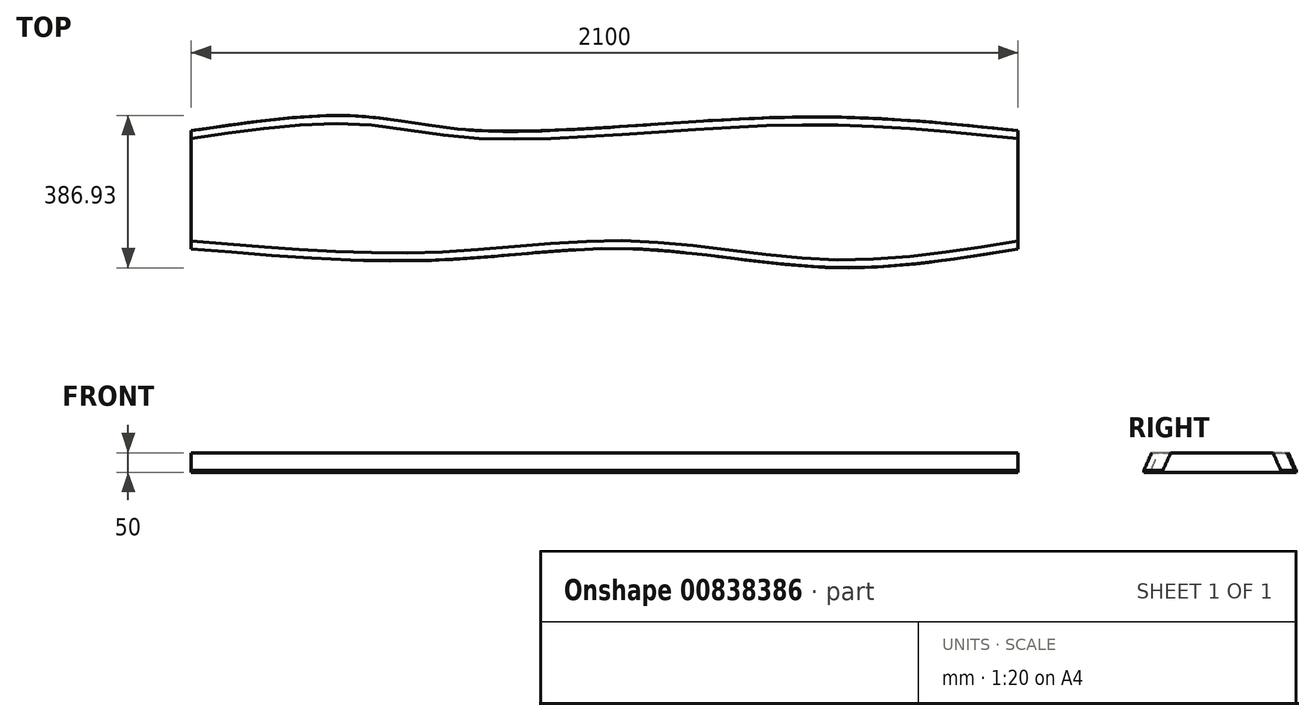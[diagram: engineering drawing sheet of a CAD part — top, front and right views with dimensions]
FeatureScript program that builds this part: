
annotation { "Feature Type Name" : "Feature", "Feature Type Description" : "" }
export const myFeature = defineFeature(function(context is Context, id is Id, definition is map)
    precondition{}
    {
        {
            var Q0;
            Q0=qCreatedBy(makeId("Top.planeOp"),FACE);
            var sketch = newSketch(context, id + "F0", { "sketchPlane" : qUnion([Q0])});
            skLineSegment(sketch, "E0.left", {"start": v(0, 0) * mm, "end": v(0, 300) * mm});
            skLineSegment(sketch, "E0.right", {"start": v(2100, 0) * mm, "end": v(2100, 300) * mm});
            skFitSpline(sketch, "E1", {"points": [v(0, 300) * mm, v(410.68, 337.9) * mm, v(739.53, 300) * mm, v(1506.84, 334.12) * mm, v(2100, 300) * mm], "startDerivative": vector(1943.02, 290.28) * mm, "endDerivative": vector(2052.76, -218.86) * mm});
            skFitSpline(sketch, "E2", {"points": [v(2100, 0) * mm, v(1627.8, -47.64) * mm, v(1117.52, 0) * mm, v(622.36, -28.74) * mm, v(0, 0) * mm], "startDerivative": vector(-1959.68, -329.58) * mm, "endDerivative": vector(-2358.67, 199.35) * mm});
            skSolve(sketch);
        }
        {
            var Q0;
            Q0 = qSketchRegion(id + "F0", true);
            extrude(context, id + "F1", {"entities" : qUnion([Q0]), "depth" : 50 * mm, "offsetDistance" : 25 * mm});
        }
        {
            var Q0;
            Q0=makeQuery(id+"F1.opExtrude","CAP_EDGE",EDGE,{"disambiguationData":[OSD([sQuery(id+"F0.wireOp",EDGE,"E2")])],"isStart":false});
            var Q1;
            Q1=makeQuery(id+"F1.opExtrude","CAP_EDGE",EDGE,{"disambiguationData":[OSD([sQuery(id+"F0.wireOp",EDGE,"E1")])],"isStart":false});
            chamfer(context, id + "F2", {"entities" : qUnion([Q0, Q1]), "chamferType" : ChamferType.TWO_OFFSETS, "width1" : 45 * mm, "oppositeDirection" : false, "width2" : 20 * mm, "tangentPropagation" : true});
        }
    });
